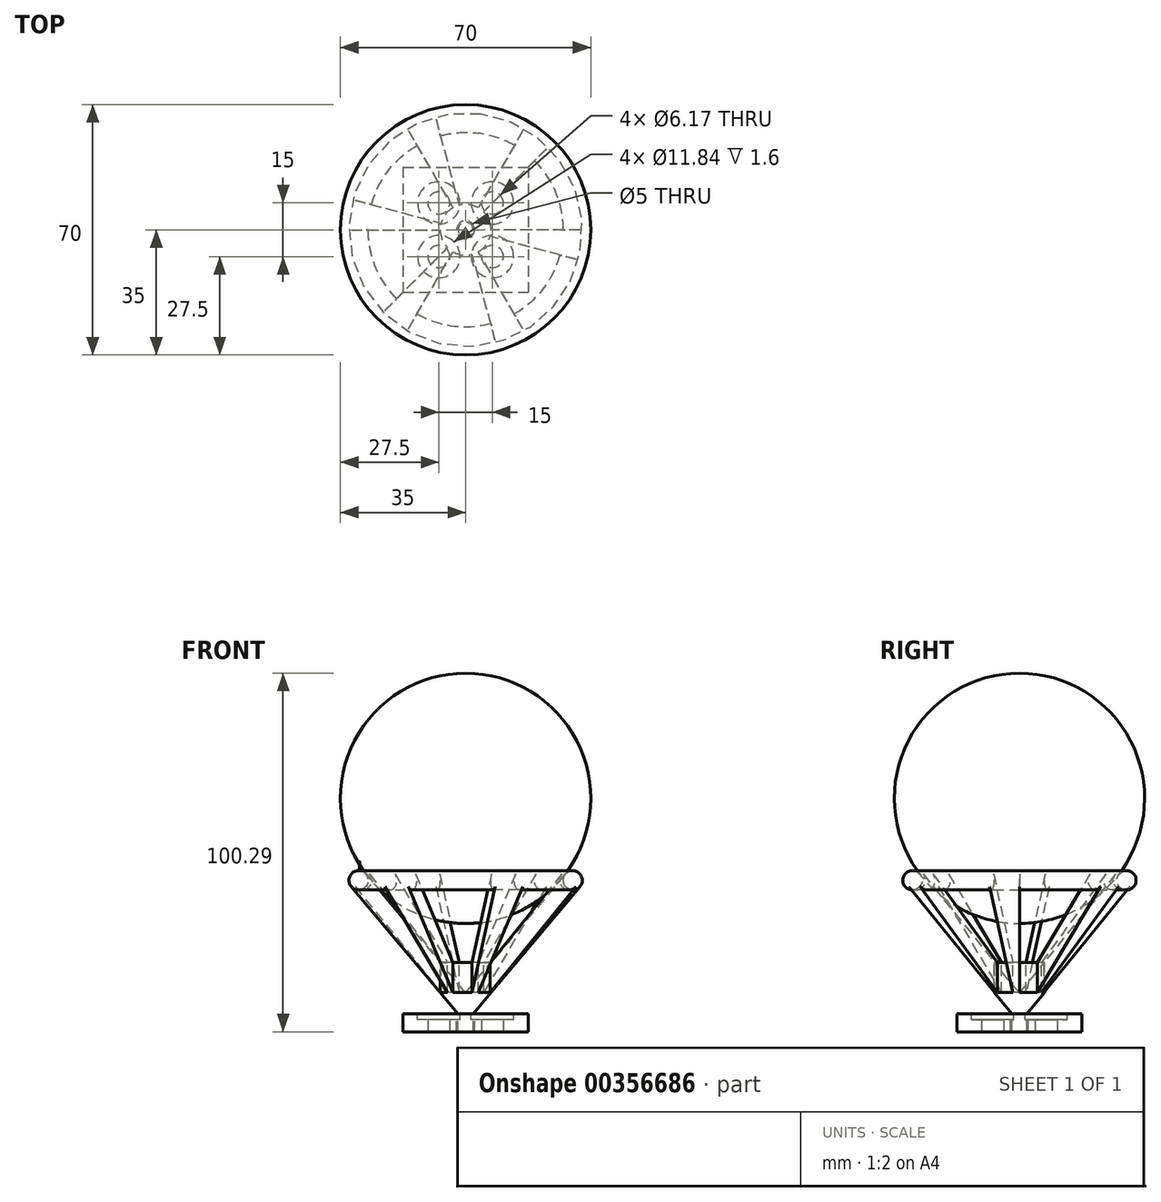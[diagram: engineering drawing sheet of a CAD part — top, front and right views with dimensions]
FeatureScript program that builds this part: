
annotation { "Feature Type Name" : "Feature", "Feature Type Description" : "" }
export const myFeature = defineFeature(function(context is Context, id is Id, definition is map)
    precondition{}
    {
        {
            var Q0;
            Q0=qCreatedBy(makeId("Top.planeOp"),FACE);
            var sketch = newSketch(context, id + "F0", { "sketchPlane" : qUnion([Q0])});
            skLineSegment(sketch, "E0.bottom", {"start": v(-17.5, 17.5) * mm, "end": v(0, 17.5) * mm});
            skLineSegment(sketch, "E0.top", {"start": v(-17.5, -17.5) * mm, "end": v(0, -17.5) * mm});
            skLineSegment(sketch, "E0.left", {"start": v(-17.5, 17.5) * mm, "end": v(-17.5, 0) * mm});
            skLineSegment(sketch, "E0.right", {"start": v(17.5, 17.5) * mm, "end": v(17.5, 0) * mm});
            skLineSegment(sketch, "E1", {"start": v(-17.5, 0) * mm, "end": v(-17.5, -17.5) * mm});
            skLineSegment(sketch, "E2", {"start": v(17.5, 0) * mm, "end": v(17.5, -17.5) * mm});
            skLineSegment(sketch, "E3", {"start": v(0, -17.5) * mm, "end": v(17.5, -17.5) * mm});
            skLineSegment(sketch, "E4", {"start": v(0, 17.5) * mm, "end": v(17.5, 17.5) * mm});
            skCircle(sketch, "E5", {"center": v(-7.5, 7.5) * mm, "radius": 3.09 * mm});
            skCircle(sketch, "E6", {"center": v(7.5, 7.5) * mm, "radius": 3.09 * mm});
            skLineSegment(sketch, "E7", {"start": v(-7.5, 7.5) * mm, "end": v(0, 7.5) * mm, "construction": true});
            skLineSegment(sketch, "E8", {"start": v(0, 7.5) * mm, "end": v(7.5, 7.5) * mm, "construction": true});
            skLineSegment(sketch, "E9", {"start": v(0, 7.5) * mm, "end": v(0, 0) * mm, "construction": true});
            skCircle(sketch, "E10.MirrorC", {"center": v(-7.5, -7.5) * mm, "radius": 3.09 * mm});
            skCircle(sketch, "E11.MirrorC", {"center": v(7.5, -7.5) * mm, "radius": 3.09 * mm});
            skSolve(sketch);
        }
        {
            var Q0;
            Q0=qSketchRegion(id+"F0",true);
            extrude(context, id + "F1", {"entities" : qUnion([Q0]), "depth" : 5 * mm});
        }
        {
            var Q0;
            Q0=makeQuery(id+"F1.opExtrude","CAP_FACE",FACE,{"disambiguationData":[OSD([sQuery(id+"F0.wireOp",EDGE,"E0.bottom"),sQuery(id+"F0.wireOp",EDGE,"E0.top"),sQuery(id+"F0.wireOp",EDGE,"E0.left"),sQuery(id+"F0.wireOp",EDGE,"E0.right"),sQuery(id+"F0.wireOp",EDGE,"E1"),sQuery(id+"F0.wireOp",EDGE,"E2"),sQuery(id+"F0.wireOp",EDGE,"E3"),sQuery(id+"F0.wireOp",EDGE,"E4"),sQuery(id+"F0.wireOp",EDGE,"E5")])],"isStart":false});
            var sketch = newSketch(context, id + "F2", { "sketchPlane" : qUnion([Q0])});
            skCircle(sketch, "E12", {"center": v(-7.5, 7.5) * mm, "radius": 5.92 * mm});
            skCircle(sketch, "E13", {"center": v(7.5, 7.5) * mm, "radius": 5.92 * mm});
            skCircle(sketch, "E14.MirrorC", {"center": v(-7.5, -7.5) * mm, "radius": 5.92 * mm});
            skCircle(sketch, "E15.MirrorC", {"center": v(7.5, -7.5) * mm, "radius": 5.92 * mm});
            skSolve(sketch);
        }
        {
            var Q0;
            Q0=qSketchRegion(id+"F2",true);
            extrude(context, id + "F3", {"entities" : qUnion([Q0]), "operationType" : NewBodyOperationType.REMOVE, "oppositeDirection" : true, "depth" : 1.6 * mm});
        }
        {
            var Q0;
            Q0=makeQuery(id+"F1.opExtrude","CAP_FACE",FACE,{"disambiguationData":[OSD([sQuery(id+"F0.wireOp",EDGE,"E0.bottom"),sQuery(id+"F0.wireOp",EDGE,"E0.top"),sQuery(id+"F0.wireOp",EDGE,"E0.left"),sQuery(id+"F0.wireOp",EDGE,"E0.right"),sQuery(id+"F0.wireOp",EDGE,"E1"),sQuery(id+"F0.wireOp",EDGE,"E2"),sQuery(id+"F0.wireOp",EDGE,"E3"),sQuery(id+"F0.wireOp",EDGE,"E4"),sQuery(id+"F0.wireOp",EDGE,"E5"),sQuery(id+"F0.wireOp",EDGE,"E6"),sQuery(id+"F0.wireOp",EDGE,"E10.MirrorC"),sQuery(id+"F0.wireOp",EDGE,"E11.MirrorC")])],"isStart":false});
            var sketch = newSketch(context, id + "F4", { "sketchPlane" : qUnion([Q0])});
            skCircle(sketch, "E16", {"center": v(0, 0) * mm, "radius": 2.5 * mm});
            skSolve(sketch);
        }
        {
            var Q0;
            Q0=qSketchRegion(id+"F4",true);
            var Q1;
            Q1=makeQuery(id+"F1.opExtrude","CAP_FACE",FACE,{"disambiguationData":[OSD([sQuery(id+"F0.wireOp",EDGE,"E0.bottom"),sQuery(id+"F0.wireOp",EDGE,"E0.top"),sQuery(id+"F0.wireOp",EDGE,"E0.left"),sQuery(id+"F0.wireOp",EDGE,"E0.right"),sQuery(id+"F0.wireOp",EDGE,"E1"),sQuery(id+"F0.wireOp",EDGE,"E2"),sQuery(id+"F0.wireOp",EDGE,"E3"),sQuery(id+"F0.wireOp",EDGE,"E4"),sQuery(id+"F0.wireOp",EDGE,"E5"),sQuery(id+"F0.wireOp",EDGE,"E6"),sQuery(id+"F0.wireOp",EDGE,"E10.MirrorC"),sQuery(id+"F0.wireOp",EDGE,"E11.MirrorC")])],"isStart":true});
            extrude(context, id + "F5", {"entities" : qUnion([Q0]), "operationType" : NewBodyOperationType.REMOVE, "endBound" : BoundingType.UP_TO_SURFACE, "oppositeDirection" : true, "endBoundEntityFace" : qUnion([Q1]), "depth" : 25 * mm});
        }
        {
            var Q0;
            Q0=qCreatedBy(makeId("Front.planeOp"),FACE);
            var sketch = newSketch(context, id + "F6", { "sketchPlane" : qUnion([Q0])});
            skLineSegment(sketch, "E17.0", {"start": v(1.58, 5) * mm, "end": v(13.42, 5) * mm, "construction": true});
            skLineSegment(sketch, "E18.0", {"start": v(-13.42, 5) * mm, "end": v(-1.58, 5) * mm, "construction": true});
            skLineSegment(sketch, "E19", {"start": v(-1.58, 5) * mm, "end": v(-31.7, 40.9) * mm, "construction": true});
            skLineSegment(sketch, "E20", {"start": v(-27.87, 44.1) * mm, "end": v(0, 10.9) * mm});
            skLineSegment(sketch, "E21", {"start": v(0, 10.9) * mm, "end": v(0, 5) * mm});
            skLineSegment(sketch, "E22", {"start": v(0, 5) * mm, "end": v(-1.58, 5) * mm, "construction": true});
            skArc(sketch, "E23.converted", {"start": v(-27.87, 44.1) * mm, "mid": v(-31.39, 44.42) * mm, "end": v(-31.7, 40.9) * mm, "construction": true});
            skLineSegment(sketch, "E24.0", {"start": v(2.5, 0) * mm, "end": v(-2.5, 0) * mm, "construction": true});
            skLineSegment(sketch, "E25", {"start": v(-32, 40.64) * mm, "end": v(-2.1, 5) * mm});
            skLineSegment(sketch, "E26", {"start": v(-2.1, 5) * mm, "end": v(-2.1, 0) * mm});
            skLineSegment(sketch, "E27", {"start": v(-2.1, 0) * mm, "end": v(0, 0) * mm});
            skLineSegment(sketch, "E28", {"start": v(0, 0) * mm, "end": v(0, 5) * mm});
            skCircle(sketch, "E29", {"center": v(-29.93, 42.37) * mm, "radius": 2.7 * mm});
            skLineSegment(sketch, "E30", {"start": v(-27.87, 44.1) * mm, "end": v(-29.93, 42.37) * mm, "construction": true});
            skLineSegment(sketch, "E31", {"start": v(-29.78, 42.5) * mm, "end": v(-29.93, 42.37) * mm, "construction": true});
            skSolve(sketch);
        }
        {
            var Q0;
            Q0=qSketchRegion(id+"F6",true);
            var Q1;
            Q1=sQuery(id+"F6.wireOp",EDGE,"E21");
            revolve(context, id + "F7", {"operationType" : NewBodyOperationType.ADD, "entities" : qUnion([Q0]), "axis" : qUnion([Q1]), "revolveType" : RevolveType.ONE_DIRECTION, "angle" : 15 * degree});
        }
        {
            var Q0;
            Q0=makeQuery(id+"F7.opRevolve","CAP_FACE",FACE,{"disambiguationData":[OSD([sQuery(id+"F6.wireOp",EDGE,"E20"),sQuery(id+"F6.wireOp",EDGE,"E21"),sQuery(id+"F6.wireOp",EDGE,"E25"),sQuery(id+"F6.wireOp",EDGE,"E26"),sQuery(id+"F6.wireOp",EDGE,"E27"),sQuery(id+"F6.wireOp",EDGE,"E28"),sQuery(id+"F6.wireOp",EDGE,"E29")])],"isStart":false});
            var sketch = newSketch(context, id + "F8", { "sketchPlane" : qUnion([Q0])});
            skLineSegment(sketch, "E32.0", {"start": v(0, 0) * mm, "end": v(0, 5) * mm});
            skLineSegment(sketch, "E32.1", {"start": v(2.1, 5) * mm, "end": v(2.1, 0) * mm});
            skLineSegment(sketch, "E32.3", {"start": v(0, 10.9) * mm, "end": v(0, 5) * mm});
            skLineSegment(sketch, "E32.4", {"start": v(7.1, 19.36) * mm, "end": v(0, 10.9) * mm});
            skLineSegment(sketch, "E32.5", {"start": v(7.1, 10.96) * mm, "end": v(2.1, 5) * mm});
            skLineSegment(sketch, "E33", {"start": v(7.1, 10.96) * mm, "end": v(7.1, 19.36) * mm});
            skCircle(sketch, "E34.converted", {"center": v(29.93, 42.37) * mm, "radius": 2.7 * mm});
            skPoint(sketch, "E35.orphan", {"position": v(27.87, 44.1) * mm});
            skPoint(sketch, "E36.orphan", {"position": v(32, 40.64) * mm});
            skLineSegment(sketch, "E37.0", {"start": v(2.1, 0) * mm, "end": v(0, 0) * mm});
            skSolve(sketch);
        }
        {
            var Q0;
            Q0=qSketchRegion(id+"F8",true);
            var Q1;
            Q1=sQuery(id+"F8.wireOp",EDGE,"E32.3");
            revolve(context, id + "F9", {"operationType" : NewBodyOperationType.ADD, "entities" : qUnion([Q0]), "axis" : qUnion([Q1]), "revolveType" : RevolveType.ONE_DIRECTION, "angle" : 45 * degree});
        }
        {
            var Q0;
            Q0=makeQuery(id+"F7.opRevolve","SWEPT_BODY",BODY,{"disambiguationData":[OSD([sQuery(id+"F6.wireOp",EDGE,"E20"),sQuery(id+"F6.wireOp",EDGE,"E21"),sQuery(id+"F6.wireOp",EDGE,"E25"),sQuery(id+"F6.wireOp",EDGE,"E26"),sQuery(id+"F6.wireOp",EDGE,"E27"),sQuery(id+"F6.wireOp",EDGE,"E28"),sQuery(id+"F6.wireOp",EDGE,"E29")])]});
            var Q1;
            Q1=makeQuery(id+"F9.boolean.opBoolean","MERGE",EDGE,{"derivedFrom":[makeQuery(id+"F7.opRevolve","CAP_EDGE",EDGE,{"disambiguationData":[OSD([sQuery(id+"F6.wireOp",EDGE,"E21"),sQuery(id+"F6.wireOp",EDGE,"E28")])],"isStart":true}),makeQuery(id+"F9.opRevolve","CAP_EDGE",EDGE,{"disambiguationData":[OSD([sQuery(id+"F8.wireOp",EDGE,"E32.0"),sQuery(id+"F8.wireOp",EDGE,"E32.3")])],"isStart":true})]});
            circularPattern(context, id + "F10", {"entities" : qUnion([Q0]), "axis" : qUnion([Q1]), "angle" : 360 * degree, "instanceCount" : 6, "equalSpace" : true});
        }
        {
            var Q0;
            Q0=makeQuery(id+"F10.opPattern","COPY",BODY,{"derivedFrom":makeQuery(id+"F7.opRevolve","SWEPT_BODY",BODY,{"disambiguationData":[OSD([sQuery(id+"F6.wireOp",EDGE,"E20"),sQuery(id+"F6.wireOp",EDGE,"E21"),sQuery(id+"F6.wireOp",EDGE,"E25"),sQuery(id+"F6.wireOp",EDGE,"E26"),sQuery(id+"F6.wireOp",EDGE,"E27"),sQuery(id+"F6.wireOp",EDGE,"E28"),sQuery(id+"F6.wireOp",EDGE,"E29")])]}),"instanceName":"5"});
            var Q1;
            Q1=makeQuery(id+"F10.opPattern","COPY",BODY,{"derivedFrom":makeQuery(id+"F7.opRevolve","SWEPT_BODY",BODY,{"disambiguationData":[OSD([sQuery(id+"F6.wireOp",EDGE,"E20"),sQuery(id+"F6.wireOp",EDGE,"E21"),sQuery(id+"F6.wireOp",EDGE,"E25"),sQuery(id+"F6.wireOp",EDGE,"E26"),sQuery(id+"F6.wireOp",EDGE,"E27"),sQuery(id+"F6.wireOp",EDGE,"E28"),sQuery(id+"F6.wireOp",EDGE,"E29")])]}),"instanceName":"4"});
            var Q2;
            Q2=makeQuery(id+"F10.opPattern","COPY",BODY,{"derivedFrom":makeQuery(id+"F7.opRevolve","SWEPT_BODY",BODY,{"disambiguationData":[OSD([sQuery(id+"F6.wireOp",EDGE,"E20"),sQuery(id+"F6.wireOp",EDGE,"E21"),sQuery(id+"F6.wireOp",EDGE,"E25"),sQuery(id+"F6.wireOp",EDGE,"E26"),sQuery(id+"F6.wireOp",EDGE,"E27"),sQuery(id+"F6.wireOp",EDGE,"E28"),sQuery(id+"F6.wireOp",EDGE,"E29")])]}),"instanceName":"3"});
            var Q3;
            Q3=makeQuery(id+"F10.opPattern","COPY",BODY,{"derivedFrom":makeQuery(id+"F7.opRevolve","SWEPT_BODY",BODY,{"disambiguationData":[OSD([sQuery(id+"F6.wireOp",EDGE,"E20"),sQuery(id+"F6.wireOp",EDGE,"E21"),sQuery(id+"F6.wireOp",EDGE,"E25"),sQuery(id+"F6.wireOp",EDGE,"E26"),sQuery(id+"F6.wireOp",EDGE,"E27"),sQuery(id+"F6.wireOp",EDGE,"E28"),sQuery(id+"F6.wireOp",EDGE,"E29")])]}),"instanceName":"2"});
            var Q4;
            Q4=makeQuery(id+"F10.opPattern","COPY",BODY,{"derivedFrom":makeQuery(id+"F7.opRevolve","SWEPT_BODY",BODY,{"disambiguationData":[OSD([sQuery(id+"F6.wireOp",EDGE,"E20"),sQuery(id+"F6.wireOp",EDGE,"E21"),sQuery(id+"F6.wireOp",EDGE,"E25"),sQuery(id+"F6.wireOp",EDGE,"E26"),sQuery(id+"F6.wireOp",EDGE,"E27"),sQuery(id+"F6.wireOp",EDGE,"E28"),sQuery(id+"F6.wireOp",EDGE,"E29")])]}),"instanceName":"1"});
            var Q5;
            Q5=makeQuery(id+"F7.opRevolve","SWEPT_BODY",BODY,{"disambiguationData":[OSD([sQuery(id+"F6.wireOp",EDGE,"E20"),sQuery(id+"F6.wireOp",EDGE,"E21"),sQuery(id+"F6.wireOp",EDGE,"E25"),sQuery(id+"F6.wireOp",EDGE,"E26"),sQuery(id+"F6.wireOp",EDGE,"E27"),sQuery(id+"F6.wireOp",EDGE,"E28"),sQuery(id+"F6.wireOp",EDGE,"E29")])]});
            booleanBodies(context, id + "F11", {"operationType" : BooleanOperationType.UNION, "tools" : qUnion([Q0, Q1, Q2, Q3, Q4, Q5])});
        }
        {
            var Q0;
            Q0=qCreatedBy(makeId("Front.planeOp"),FACE);
            var sketch = newSketch(context, id + "F12", { "sketchPlane" : qUnion([Q0])});
            skArc(sketch, "E38", {"start": v(0, 100.29) * mm, "mid": v(-35, 65.29) * mm, "end": v(0, 30.29) * mm});
            skLineSegment(sketch, "E39", {"start": v(0, 30.29) * mm, "end": v(0, 100.29) * mm});
            skArc(sketch, "E40.0", {"start": v(-32, 40.64) * mm, "mid": v(-28.2, 40.3) * mm, "end": v(-27.87, 44.1) * mm, "construction": true});
            skSolve(sketch);
        }
        {
            var Q0;
            Q0=qSketchRegion(id+"F12",true);
            var Q1;
            Q1=sQuery(id+"F12.wireOp",EDGE,"E39");
            revolve(context, id + "F13", {"entities" : qUnion([Q0]), "axis" : qUnion([Q1]), "revolveType" : RevolveType.FULL});
        }
    });
